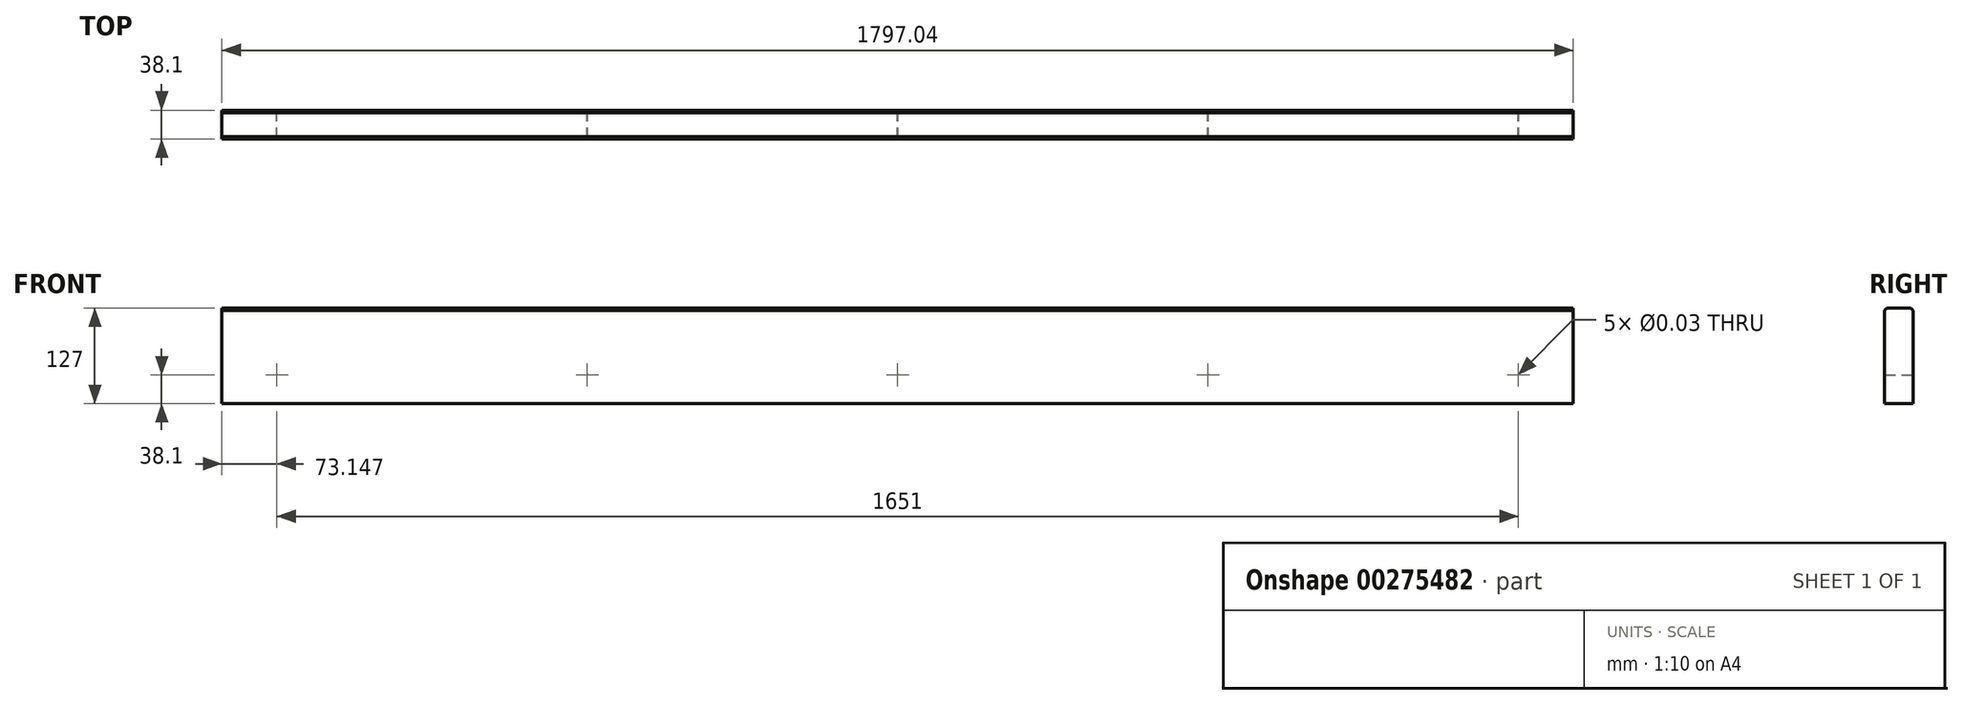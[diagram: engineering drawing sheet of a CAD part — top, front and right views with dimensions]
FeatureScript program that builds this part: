
annotation { "Feature Type Name" : "Feature", "Feature Type Description" : "" }
export const myFeature = defineFeature(function(context is Context, id is Id, definition is map)
    precondition{}
    {
        {
            var Q0;
            Q0=qCreatedBy(makeId("Right.planeOp"),FACE);
            var sketch = newSketch(context, id + "F0", { "sketchPlane" : qUnion([Q0])});
            skLineSegment(sketch, "E0.bottom", {"start": v(-19.05, 63.5) * mm, "end": v(19.05, 63.5) * mm});
            skLineSegment(sketch, "E0.top", {"start": v(-19.05, -63.5) * mm, "end": v(19.05, -63.5) * mm});
            skLineSegment(sketch, "E0.left", {"start": v(-19.05, 63.5) * mm, "end": v(-19.05, -63.5) * mm});
            skLineSegment(sketch, "E0.right", {"start": v(19.05, 63.5) * mm, "end": v(19.05, -63.5) * mm});
            skPoint(sketch, "E0.middle", {"position": v(0, 0) * mm});
            skSolve(sketch);
        }
        {
            var Q0;
            Q0 = qSketchRegion(id + "F0", true);
            extrude(context, id + "F1", {"entities" : qUnion([Q0]), "endBound" : BoundingType.SYMMETRIC, "depth" : 1797.05 * mm});
        }
        {
            var Q0;
            Q0=makeQuery(id+"F1.opExtrude","SWEPT_EDGE",EDGE,{"disambiguationData":[OSD([sQuery(id+"F0.wireOp",EDGE,"E0.bottom"),sQuery(id+"F0.wireOp",EDGE,"E0.right")])]});
            var Q1;
            Q1=makeQuery(id+"F1.opExtrude","SWEPT_EDGE",EDGE,{"disambiguationData":[OSD([sQuery(id+"F0.wireOp",EDGE,"E0.bottom"),sQuery(id+"F0.wireOp",EDGE,"E0.left")])]});
            chamfer(context, id + "F2", {"entities" : qUnion([Q0, Q1]), "width" : 3.17 * mm, "tangentPropagation" : true});
        }
        {
            var Q0;
            Q0=makeQuery(id+"F1.opExtrude","SWEPT_FACE",FACE,{"disambiguationData":[OSD([sQuery(id+"F0.wireOp",EDGE,"E0.right")])]});
            var sketch = newSketch(context, id + "F3", { "sketchPlane" : qUnion([Q0])});
            skLineSegment(sketch, "E1.0", {"start": v(-898.53, -63.5) * mm, "end": v(898.53, -63.5) * mm, "construction": true});
            skLineSegment(sketch, "E2.0", {"start": v(-898.53, -25.4) * mm, "end": v(898.53, -25.4) * mm, "construction": true});
            skLineSegment(sketch, "E3.0", {"start": v(-898.53, 60.33) * mm, "end": v(-898.53, -63.5) * mm, "construction": true});
            skLineSegment(sketch, "E4.0", {"start": v(-825.63, 60.33) * mm, "end": v(-825.63, -63.5) * mm, "construction": true});
            skPoint(sketch, "E5", {"position": v(-825.63, -25.4) * mm});
            skPoint(sketch, "E6.1.0.0", {"position": v(-412.88, -25.4) * mm});
            skPoint(sketch, "E6.2.0.0", {"position": v(-0.13, -25.4) * mm});
            skPoint(sketch, "E6.3.0.0", {"position": v(412.62, -25.4) * mm});
            skPoint(sketch, "E6.4.0.0", {"position": v(825.37, -25.4) * mm});
            skLineSegment(sketch, "E6.direction1", {"start": v(-825.63, -25.4) * mm, "end": v(-412.88, -25.4) * mm, "construction": true});
            skSolve(sketch);
        }
        {
            var Q0;
            Q0=sQuery(id+"F3.wireOp",VERTEX,"E5");
            var Q1;
            Q1=sQuery(id+"F3.wireOp",VERTEX,"E6.1.0.0");
            var Q2;
            Q2=sQuery(id+"F3.wireOp",VERTEX,"E6.2.0.0");
            var Q3;
            Q3=sQuery(id+"F3.wireOp",VERTEX,"E6.3.0.0");
            var Q4;
            Q4=sQuery(id+"F3.wireOp",VERTEX,"E6.4.0.0");
            var Q5;
            Q5=makeQuery(id+"F1.opExtrude","SWEPT_BODY",BODY,{"disambiguationData":[OSD([sQuery(id+"F0.wireOp",EDGE,"E0.bottom"),sQuery(id+"F0.wireOp",EDGE,"E0.top"),sQuery(id+"F0.wireOp",EDGE,"E0.left"),sQuery(id+"F0.wireOp",EDGE,"E0.right")])]});
            hole(context, id + "F4", {"style" : HoleStyle.SIMPLE, "endStyle" : HoleEndStyle.THROUGH, "standardTappedOrClearance" : lookupTablePath({ "standard" : "ANSI", "size" : "13/16 (0.81)", "type" : "Drilled" }), "standardBlindInLast" : lookupTablePath({ "standard" : "ANSI", "size" : "13/16", "type" : "Drilled" }), "holeDiameter" : 13 / 406.4 * mm, "tappedDepth" : 41.27 * mm, "tapClearance" : 3, "startFromSketch" : true, "locations" : qUnion([Q0, Q1, Q2, Q3, Q4]), "scope" : qUnion([Q5])});
        }
    });
